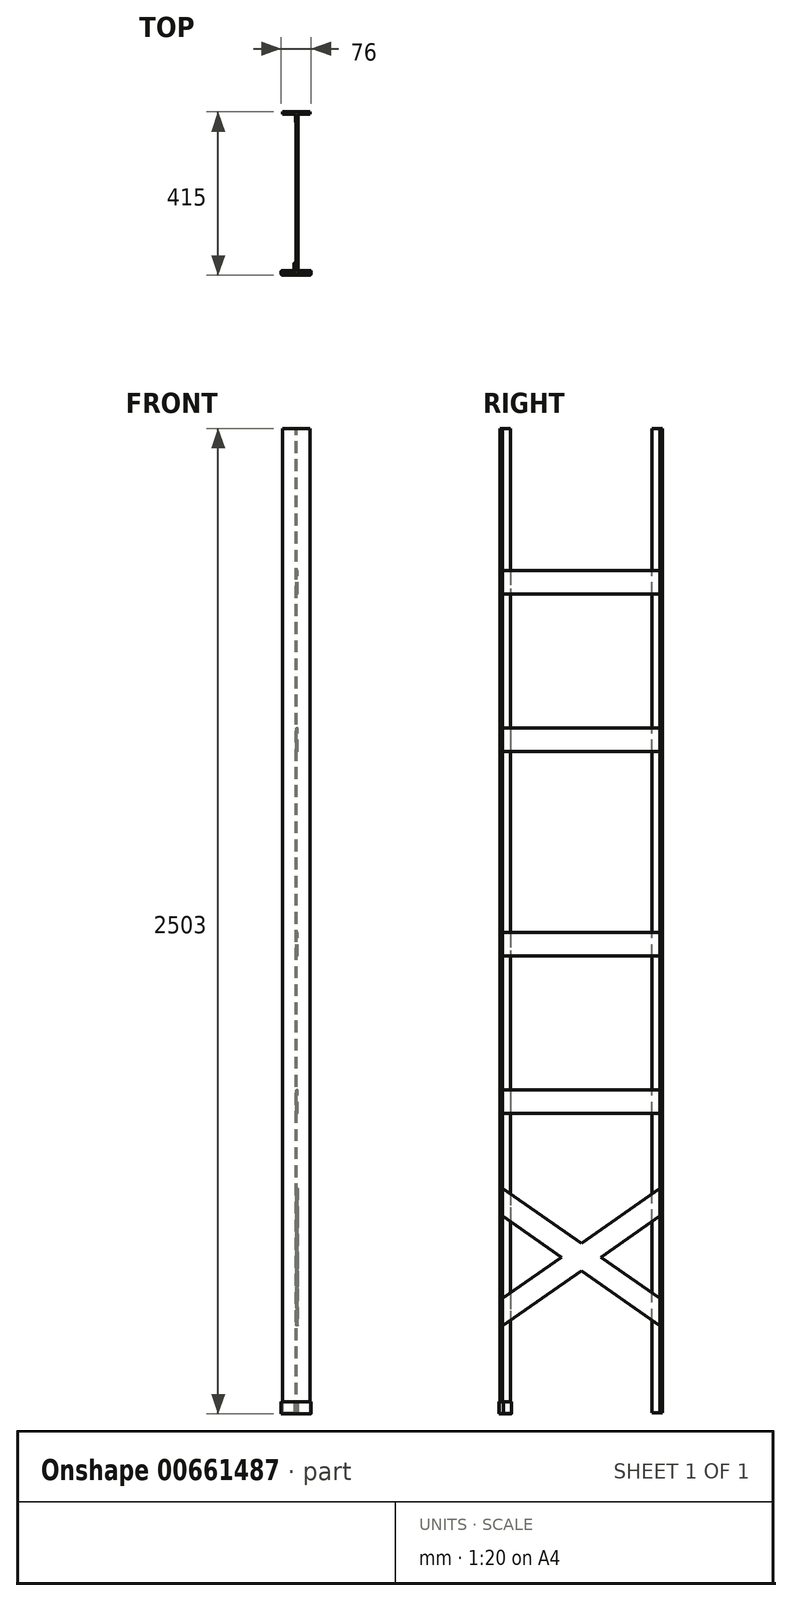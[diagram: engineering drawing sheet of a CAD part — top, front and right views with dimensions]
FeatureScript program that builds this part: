
annotation { "Feature Type Name" : "Feature", "Feature Type Description" : "" }
export const myFeature = defineFeature(function(context is Context, id is Id, definition is map)
    precondition{}
    {
        {
            var Q0;
            Q0=qCreatedBy(makeId("Top.planeOp"),FACE);
            var sketch = newSketch(context, id + "F0", { "sketchPlane" : qUnion([Q0])});
            skLineSegment(sketch, "E0", {"start": v(0, 20) * mm, "end": v(-2, 20) * mm});
            skLineSegment(sketch, "E1", {"start": v(-2, 20) * mm, "end": v(-2, 0) * mm});
            skLineSegment(sketch, "E2", {"start": v(-2, 0) * mm, "end": v(-35, 0) * mm});
            skLineSegment(sketch, "E3", {"start": v(-35, 0) * mm, "end": v(-35, -6) * mm});
            skLineSegment(sketch, "E4", {"start": v(-35, -6) * mm, "end": v(0, -6) * mm});
            skLineSegment(sketch, "E5.MirrorCS", {"start": v(35, 0) * mm, "end": v(35, -6) * mm});
            skLineSegment(sketch, "E6.MirrorCS", {"start": v(2, 20) * mm, "end": v(2, 0) * mm});
            skLineSegment(sketch, "E7.MirrorCS", {"start": v(2, 0) * mm, "end": v(35, 0) * mm});
            skLineSegment(sketch, "E8.MirrorCS", {"start": v(0, 20) * mm, "end": v(2, 20) * mm});
            skLineSegment(sketch, "E9.MirrorCS", {"start": v(35, -6) * mm, "end": v(0, -6) * mm});
            skSolve(sketch);
        }
        {
            var Q0;
            Q0=makeQuery(id+"F0.imprint","IMPRINT",FACE,{"disambiguationData":[TD([[makeQuery(id+"F0.imprint","IMPRINT",EDGE,{"derivedFrom":sQuery(id+"F0.wireOp",EDGE,"E0")}),1.0]])]});
            extrude(context, id + "F1", {"entities" : qUnion([Q0]), "depth" : 2500 * mm, "offsetDistance" : 25 * mm});
        }
        {
            var Q0;
            Q0=makeQuery(id+"F1.opExtrude","SWEPT_BODY",BODY,{"disambiguationData":[OSD([sQuery(id+"F0.wireOp",EDGE,"E0"),sQuery(id+"F0.wireOp",EDGE,"E1"),sQuery(id+"F0.wireOp",EDGE,"E2"),sQuery(id+"F0.wireOp",EDGE,"E3"),sQuery(id+"F0.wireOp",EDGE,"E4"),sQuery(id+"F0.wireOp",EDGE,"E5.MirrorCS"),sQuery(id+"F0.wireOp",EDGE,"E6.MirrorCS"),sQuery(id+"F0.wireOp",EDGE,"E7.MirrorCS"),sQuery(id+"F0.wireOp",EDGE,"E8.MirrorCS"),sQuery(id+"F0.wireOp",EDGE,"E9.MirrorCS")])]});
            var Q1;
            Q1=qCreatedBy(makeId("Front.planeOp"),FACE);
            transform(context, id + "F2", {"entities" : qUnion([Q0]), "transformType" : TransformType.TRANSLATION_DISTANCE, "transformDirection" : qUnion([Q1]), "distance" : 412 * mm, "oppositeDirection" : true, "makeCopy" : true});
        }
        {
            var Q0;
            Q0=makeQuery(id+"F2.opPattern","COPY",BODY,{"derivedFrom":makeQuery(id+"F1.opExtrude","SWEPT_BODY",BODY,{"disambiguationData":[OSD([sQuery(id+"F0.wireOp",EDGE,"E0"),sQuery(id+"F0.wireOp",EDGE,"E1"),sQuery(id+"F0.wireOp",EDGE,"E2"),sQuery(id+"F0.wireOp",EDGE,"E3"),sQuery(id+"F0.wireOp",EDGE,"E4"),sQuery(id+"F0.wireOp",EDGE,"E5.MirrorCS"),sQuery(id+"F0.wireOp",EDGE,"E6.MirrorCS"),sQuery(id+"F0.wireOp",EDGE,"E7.MirrorCS"),sQuery(id+"F0.wireOp",EDGE,"E8.MirrorCS"),sQuery(id+"F0.wireOp",EDGE,"E9.MirrorCS")])]}),"instanceName":"1"});
            var Q1;
            Q1=makeQuery(id+"F2.opPattern","COPY",EDGE,{"derivedFrom":makeQuery(id+"F1.opExtrude","CAP_EDGE",EDGE,{"disambiguationData":[OSD([sQuery(id+"F0.wireOp",EDGE,"E4"),sQuery(id+"F0.wireOp",EDGE,"E9.MirrorCS")])],"isStart":false}),"instanceName":"1"});
            transform(context, id + "F3", {"entities" : qUnion([Q0]), "transformType" : TransformType.ROTATION, "transformAxis" : qUnion([Q1]), "angle" : 180 * degree, "makeCopy" : false});
        }
        {
            var Q0;
            Q0=makeQuery(id+"F2.opPattern","COPY",BODY,{"derivedFrom":makeQuery(id+"F1.opExtrude","SWEPT_BODY",BODY,{"disambiguationData":[OSD([sQuery(id+"F0.wireOp",EDGE,"E0"),sQuery(id+"F0.wireOp",EDGE,"E1"),sQuery(id+"F0.wireOp",EDGE,"E2"),sQuery(id+"F0.wireOp",EDGE,"E3"),sQuery(id+"F0.wireOp",EDGE,"E4"),sQuery(id+"F0.wireOp",EDGE,"E5.MirrorCS"),sQuery(id+"F0.wireOp",EDGE,"E6.MirrorCS"),sQuery(id+"F0.wireOp",EDGE,"E7.MirrorCS"),sQuery(id+"F0.wireOp",EDGE,"E8.MirrorCS"),sQuery(id+"F0.wireOp",EDGE,"E9.MirrorCS")])]}),"instanceName":"1"});
            var Q1;
            Q1=qCreatedBy(makeId("Top.planeOp"),FACE);
            transform(context, id + "F4", {"entities" : qUnion([Q0]), "transformType" : TransformType.TRANSLATION_DISTANCE, "transformDirection" : qUnion([Q1]), "distance" : 2500 * mm, "oppositeDirection" : true, "makeCopy" : false});
        }
        {
            var Q0;
            Q0=qCreatedBy(makeId("Right.planeOp"),FACE);
            var sketch = newSketch(context, id + "F5", { "sketchPlane" : qUnion([Q0])});
            skLineSegment(sketch, "E10", {"start": v(0, 0) * mm, "end": v(0, 70) * mm});
            skLineSegment(sketch, "E11", {"start": v(0, 70) * mm, "end": v(400, 350) * mm});
            skLineSegment(sketch, "E12", {"start": v(400, 350) * mm, "end": v(400, 280) * mm});
            skLineSegment(sketch, "E13", {"start": v(400, 280) * mm, "end": v(0, 0) * mm});
            skLineSegment(sketch, "E14", {"start": v(400.11, 0) * mm, "end": v(0, 280) * mm});
            skLineSegment(sketch, "E15", {"start": v(0, 280) * mm, "end": v(0, 350) * mm});
            skLineSegment(sketch, "E16", {"start": v(0, 350) * mm, "end": v(400.11, 70) * mm});
            skLineSegment(sketch, "E17", {"start": v(400.11, 70) * mm, "end": v(400.11, 0) * mm});
            skSolve(sketch);
        }
        {
            var Q0;
            Q0 = qSketchRegion(id + "F5", true);
            extrude(context, id + "F6", {"entities" : qUnion([Q0]), "depth" : 5 * mm, "offsetDistance" : 25 * mm});
        }
        {
            var Q0;
            Q0=makeQuery(id+"F6.opExtrude","SWEPT_BODY",BODY,{"disambiguationData":[OSD([sQuery(id+"F5.wireOp",EDGE,"E10"),sQuery(id+"F5.wireOp",EDGE,"E11"),sQuery(id+"F5.wireOp",EDGE,"E12"),sQuery(id+"F5.wireOp",EDGE,"E13"),sQuery(id+"F5.wireOp",EDGE,"E14"),sQuery(id+"F5.wireOp",EDGE,"E15"),sQuery(id+"F5.wireOp",EDGE,"E16"),sQuery(id+"F5.wireOp",EDGE,"E17")])]});
            var Q1;
            Q1=qCreatedBy(makeId("Top.planeOp"),FACE);
            transform(context, id + "F7", {"entities" : qUnion([Q0]), "transformType" : TransformType.TRANSLATION_DISTANCE, "transformDirection" : qUnion([Q1]), "distance" : 220 * mm, "makeCopy" : false});
        }
        {
            var Q0;
            Q0=qCreatedBy(makeId("Right.planeOp"),FACE);
            var sketch = newSketch(context, id + "F8", { "sketchPlane" : qUnion([Q0])});
            skLineSegment(sketch, "E18.bottom", {"start": v(400, 0) * mm, "end": v(0, 0) * mm});
            skLineSegment(sketch, "E18.top", {"start": v(400, 60) * mm, "end": v(0, 60) * mm});
            skLineSegment(sketch, "E18.left", {"start": v(400, 0) * mm, "end": v(400, 60) * mm});
            skLineSegment(sketch, "E18.right", {"start": v(0, 0) * mm, "end": v(0, 60) * mm});
            skSolve(sketch);
        }
        {
            var Q0;
            Q0 = qSketchRegion(id + "F8", true);
            extrude(context, id + "F9", {"entities" : qUnion([Q0]), "depth" : 5 * mm, "offsetDistance" : 25 * mm});
        }
        {
            var Q0;
            Q0=makeQuery(id+"F9.opExtrude","SWEPT_BODY",BODY,{"disambiguationData":[OSD([sQuery(id+"F8.wireOp",EDGE,"E18.bottom"),sQuery(id+"F8.wireOp",EDGE,"E18.top"),sQuery(id+"F8.wireOp",EDGE,"E18.left"),sQuery(id+"F8.wireOp",EDGE,"E18.right")])]});
            var Q1;
            Q1=qCreatedBy(makeId("Top.planeOp"),FACE);
            transform(context, id + "F10", {"entities" : qUnion([Q0]), "transformType" : TransformType.TRANSLATION_DISTANCE, "transformDirection" : qUnion([Q1]), "distance" : 760 * mm, "makeCopy" : true});
        }
        {
            var Q0;
            Q0=makeQuery(id+"F9.opExtrude","SWEPT_BODY",BODY,{"disambiguationData":[OSD([sQuery(id+"F8.wireOp",EDGE,"E18.bottom"),sQuery(id+"F8.wireOp",EDGE,"E18.top"),sQuery(id+"F8.wireOp",EDGE,"E18.left"),sQuery(id+"F8.wireOp",EDGE,"E18.right")])]});
            var Q1;
            Q1=qCreatedBy(makeId("Top.planeOp"),FACE);
            transform(context, id + "F11", {"entities" : qUnion([Q0]), "transformType" : TransformType.TRANSLATION_DISTANCE, "transformDirection" : qUnion([Q1]), "distance" : 1160 * mm, "makeCopy" : true});
        }
        {
            var Q0;
            Q0=makeQuery(id+"F9.opExtrude","SWEPT_BODY",BODY,{"disambiguationData":[OSD([sQuery(id+"F8.wireOp",EDGE,"E18.bottom"),sQuery(id+"F8.wireOp",EDGE,"E18.top"),sQuery(id+"F8.wireOp",EDGE,"E18.left"),sQuery(id+"F8.wireOp",EDGE,"E18.right")])]});
            var Q1;
            Q1=qCreatedBy(makeId("Top.planeOp"),FACE);
            transform(context, id + "F12", {"entities" : qUnion([Q0]), "transformType" : TransformType.TRANSLATION_DISTANCE, "transformDirection" : qUnion([Q1]), "distance" : 1680 * mm, "makeCopy" : true});
        }
        {
            var Q0;
            Q0=makeQuery(id+"F9.opExtrude","SWEPT_BODY",BODY,{"disambiguationData":[OSD([sQuery(id+"F8.wireOp",EDGE,"E18.bottom"),sQuery(id+"F8.wireOp",EDGE,"E18.top"),sQuery(id+"F8.wireOp",EDGE,"E18.left"),sQuery(id+"F8.wireOp",EDGE,"E18.right")])]});
            var Q1;
            Q1=qCreatedBy(makeId("Top.planeOp"),FACE);
            transform(context, id + "F13", {"entities" : qUnion([Q0]), "transformType" : TransformType.TRANSLATION_DISTANCE, "transformDirection" : qUnion([Q1]), "distance" : 2080 * mm, "makeCopy" : false});
        }
        {
            var Q0;
            Q0=qCreatedBy(makeId("Top.planeOp"),FACE);
            var sketch = newSketch(context, id + "F14", { "sketchPlane" : qUnion([Q0])});
            skLineSegment(sketch, "E19", {"start": v(-38, -0.68) * mm, "end": v(-38, -6) * mm});
            skLineSegment(sketch, "E20", {"start": v(-35, -9) * mm, "end": v(35, -9) * mm});
            skLineSegment(sketch, "E21", {"start": v(38, -6) * mm, "end": v(38, 0) * mm});
            skLineSegment(sketch, "E22", {"start": v(35, 3) * mm, "end": v(8, 3) * mm});
            skLineSegment(sketch, "E23", {"start": v(5, 6) * mm, "end": v(5, 20) * mm});
            skLineSegment(sketch, "E24", {"start": v(2, 23) * mm, "end": v(-2, 23) * mm});
            skLineSegment(sketch, "E25", {"start": v(-5, 20) * mm, "end": v(-5, 6) * mm});
            skLineSegment(sketch, "E26", {"start": v(-8, 3) * mm, "end": v(-35, 3) * mm});
            skLineSegment(sketch, "E27", {"start": v(-38, 0) * mm, "end": v(-38, -0.68) * mm});
            skPoint(sketch, "E28.visualSharp", {"position": v(-5, 3) * mm});
            skArc(sketch, "E28.filletArc", {"start": v(-8, 3) * mm, "mid": v(-5.88, 3.88) * mm, "end": v(-5, 6) * mm});
            skPoint(sketch, "E29.visualSharp", {"position": v(5, 3) * mm});
            skArc(sketch, "E29.filletArc", {"start": v(5, 6) * mm, "mid": v(5.88, 3.88) * mm, "end": v(8, 3) * mm});
            skPoint(sketch, "E30.visualSharp", {"position": v(5, 23) * mm});
            skArc(sketch, "E30.filletArc", {"start": v(5, 20) * mm, "mid": v(4.12, 22.12) * mm, "end": v(2, 23) * mm});
            skPoint(sketch, "E31.visualSharp", {"position": v(-5, 23) * mm});
            skArc(sketch, "E31.filletArc", {"start": v(-2, 23) * mm, "mid": v(-4.12, 22.12) * mm, "end": v(-5, 20) * mm});
            skPoint(sketch, "E32.visualSharp", {"position": v(-38, 3) * mm});
            skArc(sketch, "E32.filletArc", {"start": v(-35, 3) * mm, "mid": v(-37.12, 2.12) * mm, "end": v(-38, 0) * mm});
            skPoint(sketch, "E33.visualSharp", {"position": v(-38, -9) * mm});
            skArc(sketch, "E33.filletArc", {"start": v(-38, -6) * mm, "mid": v(-37.12, -8.12) * mm, "end": v(-35, -9) * mm});
            skPoint(sketch, "E34.visualSharp", {"position": v(38, -9) * mm});
            skArc(sketch, "E34.filletArc", {"start": v(35, -9) * mm, "mid": v(37.12, -8.12) * mm, "end": v(38, -6) * mm});
            skPoint(sketch, "E35.visualSharp", {"position": v(38, 3) * mm});
            skArc(sketch, "E35.filletArc", {"start": v(38, 0) * mm, "mid": v(37.12, 2.12) * mm, "end": v(35, 3) * mm});
            skSolve(sketch);
        }
        {
            var Q0;
            Q0 = qSketchRegion(id + "F14", true);
            extrude(context, id + "F15", {"entities" : qUnion([Q0]), "depth" : 30 * mm, "offsetDistance" : 25 * mm});
        }
        {
            var Q0;
            Q0=makeQuery(id+"F15.opExtrude","SWEPT_BODY",BODY,{"disambiguationData":[OSD([sQuery(id+"F14.wireOp",EDGE,"E19"),sQuery(id+"F14.wireOp",EDGE,"E20"),sQuery(id+"F14.wireOp",EDGE,"E21"),sQuery(id+"F14.wireOp",EDGE,"E22"),sQuery(id+"F14.wireOp",EDGE,"E23"),sQuery(id+"F14.wireOp",EDGE,"E24"),sQuery(id+"F14.wireOp",EDGE,"E25"),sQuery(id+"F14.wireOp",EDGE,"E26"),sQuery(id+"F14.wireOp",EDGE,"E27"),sQuery(id+"F14.wireOp",EDGE,"E28.filletArc"),sQuery(id+"F14.wireOp",EDGE,"E29.filletArc"),sQuery(id+"F14.wireOp",EDGE,"E30.filletArc"),sQuery(id+"F14.wireOp",EDGE,"E31.filletArc"),sQuery(id+"F14.wireOp",EDGE,"E32.filletArc"),sQuery(id+"F14.wireOp",EDGE,"E33.filletArc"),sQuery(id+"F14.wireOp",EDGE,"E34.filletArc"),sQuery(id+"F14.wireOp",EDGE,"E35.filletArc")])]});
            var Q1;
            Q1=qCreatedBy(makeId("Top.planeOp"),FACE);
            transform(context, id + "F16", {"entities" : qUnion([Q0]), "transformType" : TransformType.TRANSLATION_DISTANCE, "transformDirection" : qUnion([Q1]), "distance" : 3 * mm, "oppositeDirection" : true, "makeCopy" : false});
        }
        {
            var Q0;
            Q0=makeQuery(id+"F1.opExtrude","SWEPT_BODY",BODY,{"disambiguationData":[OSD([sQuery(id+"F0.wireOp",EDGE,"E0"),sQuery(id+"F0.wireOp",EDGE,"E1"),sQuery(id+"F0.wireOp",EDGE,"E2"),sQuery(id+"F0.wireOp",EDGE,"E3"),sQuery(id+"F0.wireOp",EDGE,"E4"),sQuery(id+"F0.wireOp",EDGE,"E5.MirrorCS"),sQuery(id+"F0.wireOp",EDGE,"E6.MirrorCS"),sQuery(id+"F0.wireOp",EDGE,"E7.MirrorCS"),sQuery(id+"F0.wireOp",EDGE,"E8.MirrorCS"),sQuery(id+"F0.wireOp",EDGE,"E9.MirrorCS")])]});
            var Q1;
            Q1=makeQuery(id+"F15.opExtrude","SWEPT_BODY",BODY,{"disambiguationData":[OSD([sQuery(id+"F14.wireOp",EDGE,"E19"),sQuery(id+"F14.wireOp",EDGE,"E20"),sQuery(id+"F14.wireOp",EDGE,"E21"),sQuery(id+"F14.wireOp",EDGE,"E22"),sQuery(id+"F14.wireOp",EDGE,"E23"),sQuery(id+"F14.wireOp",EDGE,"E24"),sQuery(id+"F14.wireOp",EDGE,"E25"),sQuery(id+"F14.wireOp",EDGE,"E26"),sQuery(id+"F14.wireOp",EDGE,"E27"),sQuery(id+"F14.wireOp",EDGE,"E28.filletArc"),sQuery(id+"F14.wireOp",EDGE,"E29.filletArc"),sQuery(id+"F14.wireOp",EDGE,"E30.filletArc"),sQuery(id+"F14.wireOp",EDGE,"E31.filletArc"),sQuery(id+"F14.wireOp",EDGE,"E32.filletArc"),sQuery(id+"F14.wireOp",EDGE,"E33.filletArc"),sQuery(id+"F14.wireOp",EDGE,"E34.filletArc"),sQuery(id+"F14.wireOp",EDGE,"E35.filletArc")])]});
            booleanBodies(context, id + "F17", {"operationType" : BooleanOperationType.SUBTRACTION, "tools" : qUnion([Q0]), "targets" : qUnion([Q1]), "keepTools" : true});
        }
    });
